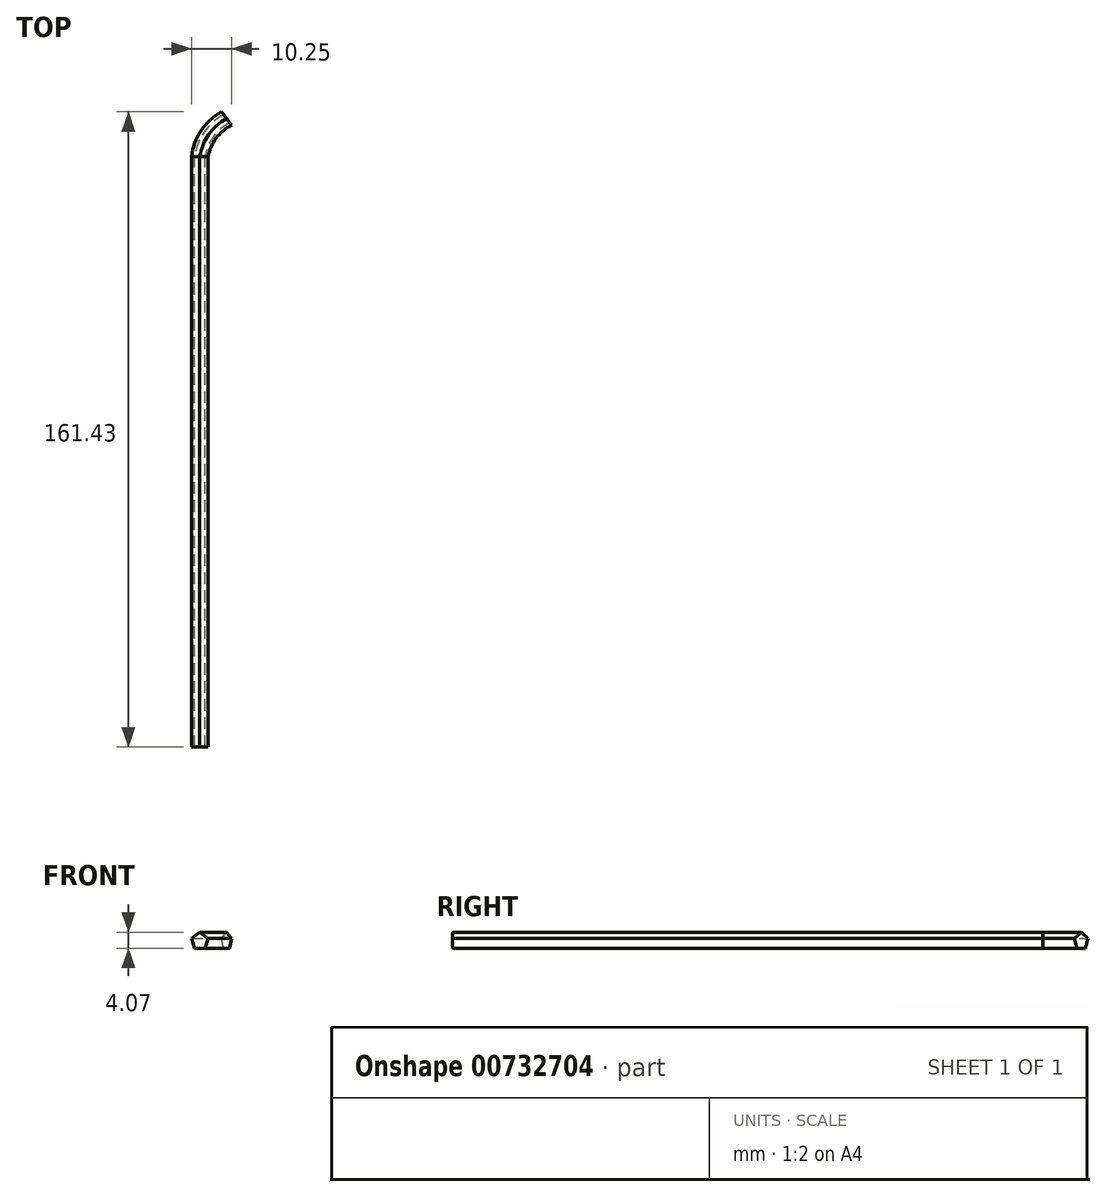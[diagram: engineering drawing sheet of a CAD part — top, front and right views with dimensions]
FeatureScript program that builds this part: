
annotation { "Feature Type Name" : "Feature", "Feature Type Description" : "" }
export const myFeature = defineFeature(function(context is Context, id is Id, definition is map)
    precondition{}
    {
        {
            var Q0;
            Q0=qCreatedBy(makeId("Front.planeOp"),FACE);
            var sketch = newSketch(context, id + "F0", { "sketchPlane" : qUnion([Q0])});
            skCircle(sketch, "E0.cCircle", {"center": v(0, 0) * mm, "radius": 2.25 * mm, "construction": true});
            skLineSegment(sketch, "E0.0", {"start": v(0, 2.25) * mm, "end": v(2.14, 0.7) * mm});
            skLineSegment(sketch, "E0.1", {"start": v(2.14, 0.7) * mm, "end": v(1.32, -1.82) * mm});
            skLineSegment(sketch, "E0.2", {"start": v(1.32, -1.82) * mm, "end": v(-1.32, -1.82) * mm});
            skLineSegment(sketch, "E0.3", {"start": v(-1.32, -1.82) * mm, "end": v(-2.14, 0.7) * mm});
            skLineSegment(sketch, "E0.4", {"start": v(-2.14, 0.7) * mm, "end": v(0, 2.25) * mm});
            skSolve(sketch);
        }
        {
            var Q0;
            Q0=makeQuery(id+"F0.imprint","IMPRINT",FACE,{"disambiguationData":[TD([[makeQuery(id+"F0.imprint","IMPRINT",EDGE,{"derivedFrom":sQuery(id+"F0.wireOp",EDGE,"E0.0")}),-1.0]])]});
            extrude(context, id + "F1", {"entities" : qUnion([Q0]), "depth" : 150 * mm, "offsetDistance" : 25 * mm});
        }
        {
            var Q0;
            Q0=qCreatedBy(makeId("Top.planeOp"),FACE);
            var sketch = newSketch(context, id + "F2", { "sketchPlane" : qUnion([Q0])});
            skArc(sketch, "E1", {"start": v(6.83, 9.72) * mm, "mid": v(2.26, 5.67) * mm, "end": v(0, 0) * mm});
            skSolve(sketch);
        }
        {
            var Q0;
            Q0=makeQuery(id+"F1.opExtrude","CAP_FACE",FACE,{"disambiguationData":[OSD([sQuery(id+"F0.wireOp",EDGE,"E0.0"),sQuery(id+"F0.wireOp",EDGE,"E0.1"),sQuery(id+"F0.wireOp",EDGE,"E0.2"),sQuery(id+"F0.wireOp",EDGE,"E0.3"),sQuery(id+"F0.wireOp",EDGE,"E0.4")])],"isStart":true});
            var Q1;
            Q1=sQuery(id+"F2.wireOp",EDGE,"E1");
            sweep(context, id + "F3", {"operationType" : NewBodyOperationType.ADD, "profiles" : qUnion([Q0]), "path" : qUnion([Q1])});
        }
    });
